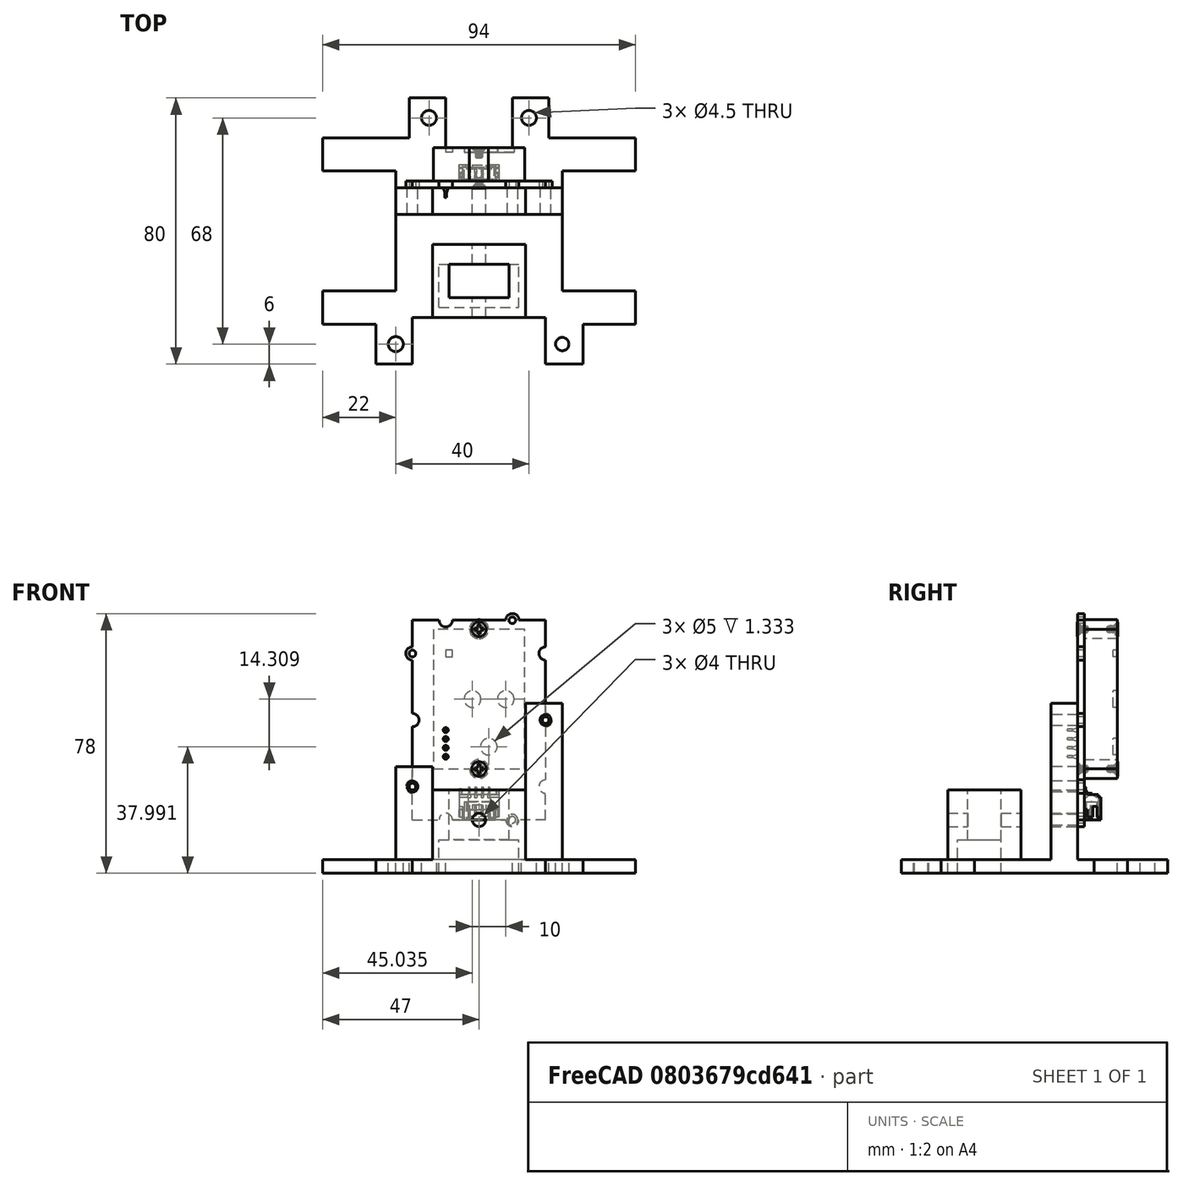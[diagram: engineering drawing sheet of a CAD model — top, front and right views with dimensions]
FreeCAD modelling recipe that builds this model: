
FCSTD DOCUMENT  (FreeCAD 0.20R29177 (Git))
Label: spin07012022
License: All rights reserved
LicenseURL: http://en.wikipedia.org/wiki/All_rights_reserved
objects: Part::Box×15, Part::Cylinder×9, Part::MultiFuse×5, Part::Cut×3, Part::Feature×1
note: 33 computed .brp shape members not serialized (recipe doc carries the construction recipe); baked Part::Feature solids carry a one-line shape summary decoded from their .brp

FEATURE [Part::Cylinder] Cylinder103  label="Cylinder107"
  Angle = 360
  AttacherType = Attacher::AttachEngine3D
  FirstAngle = 0
  Height = 10
  Placement = pos=(62,3,0) rot=(0,0,1;0rad)
  Radius = 2.25
  SecondAngle = 0
FEATURE [Part::Box] Box064  label="base005"
  AttacherType = Attacher::AttachEngine3D
  Height = 4
  Length = 26
  Placement = pos=(-10.25,68,0) rot=(0,0,1;0rad)
  Width = 12
FEATURE [Part::Box] Box060  label="base001"
  AttacherType = Attacher::AttachEngine3D
  Height = 4
  Length = 94
  Width = 80
FEATURE [Part::Box] Box061  label="base002"
  AttacherType = Attacher::AttachEngine3D
  Height = 4
  Length = 26
  Width = 12
FEATURE [Part::Box] Box062  label="base003"
  AttacherType = Attacher::AttachEngine3D
  Height = 4
  Length = 26
  Placement = pos=(68,0,0) rot=(0,0,1;0rad)
  Width = 12
FEATURE [Part::Cylinder] Cylinder104  label="Cylinder103"
  Angle = 360
  AttacherType = Attacher::AttachEngine3D
  FirstAngle = 0
  Height = 10
  Placement = pos=(72,71,0) rot=(0,0,1;0rad)
  Radius = 2.25
  SecondAngle = 0
FEATURE [Part::Cylinder] Cylinder106  label="Cylinder104"
  Angle = 360
  AttacherType = Attacher::AttachEngine3D
  FirstAngle = 0
  Height = 10
  Placement = pos=(22,71,0) rot=(0,0,1;0rad)
  Radius = 2
  SecondAngle = 0
FEATURE [Part::Cylinder] Cylinder105  label="Cylinder108"
  Angle = 360
  AttacherType = Attacher::AttachEngine3D
  FirstAngle = 0
  Height = 10
  Placement = pos=(32,3,0) rot=(0,0,1;0rad)
  Radius = 2.25
  SecondAngle = 0
FEATURE [Part::Box] Box081  label="Cube039"
  AttacherType = Attacher::AttachEngine3D
  Height = 10
  Length = 25
  Placement = pos=(85,26,140) rot=(0,0,1;0rad)
  Width = 36
FEATURE [Part::Box] Box082  label="Cube040"
  AttacherType = Attacher::AttachEngine3D
  Height = 10
  Length = 40
  Placement = pos=(40,1,140) rot=(0,0,1;0rad)
  Width = 17
FEATURE [Part::Box] Box073  label="baseSpineCut"
  AttacherType = Attacher::AttachEngine3D
  Height = 25
  Length = 18
  Placement = pos=(51,24,140) rot=(0,0,1;0rad)
  Width = 10
FEATURE [Part::Cylinder] Cylinder107  label="Cylinder109"
  Angle = 360
  AttacherType = Attacher::AttachEngine3D
  FirstAngle = 0
  Height = 10
  Radius = 1
  SecondAngle = 0
FEATURE [Part::MultiFuse] Fusion123  label="screwIns001"
  Placement = pos=(0,3,0) rot=(0,0,1;0rad)
  Shapes = -> [Cylinder105,Cylinder107,Cylinder103,Cylinder104,Cylinder106]
FEATURE [Part::Box] Box080  label="Cube038"
  AttacherType = Attacher::AttachEngine3D
  Height = 10
  Length = 22
  Placement = pos=(13,26,140) rot=(0,0,1;0rad)
  Width = 36
FEATURE [Part::Box] Box063  label="base004"
  AttacherType = Attacher::AttachEngine3D
  Height = 4
  Length = 26
  Placement = pos=(78,68,0) rot=(0,0,1;0rad)
  Width = 12
FEATURE [Part::MultiFuse] Fusion122
  Shapes = -> [Box064,Box063,Box061,Box062]
FEATURE [Part::Cut] Cut019  label="baseNew"
  Base = -> Box060
  Tool = -> Fusion122
FEATURE [Part::Cut] Cut020  label="baseNew001"
  Base = -> Cut019
  Placement = pos=(107,84,140) rot=(0,0,1;3.14159rad)
  Tool = -> Fusion123
FEATURE [Part::Box] Box083  label="Cube041"
  AttacherType = Attacher::AttachEngine3D
  Height = 10
  Length = 24
  Placement = pos=(48,21,140) rot=(0,0,1;0rad)
  Width = 13
FEATURE [Part::Box] Box084  label="Cube042"
  AttacherType = Attacher::AttachEngine3D
  Height = 51
  Length = 50
  Placement = pos=(35,49,140) rot=(0,0,1;0rad)
  Width = 8
FEATURE [Part::Box] Box085  label="Cube043"
  AttacherType = Attacher::AttachEngine3D
  Height = 10
  Length = 15
  Placement = pos=(70,69,140) rot=(0,0,1;1.5708rad)
  Width = 20
FEATURE [Part::Box] Box086  label="baseSpineIn"
  AttacherType = Attacher::AttachEngine3D
  Height = 25
  Length = 28
  Placement = pos=(46,18,140) rot=(0,0,1;0rad)
  Width = 22
FEATURE [Part::Cylinder] Cylinder
  Angle = 360
  AttacherType = Attacher::AttachEngine3D
  FirstAngle = 0
  Height = 50
  Placement = pos=(60,17,156) rot=(-1,0,0;1.5708rad)
  Radius = 2
  SecondAngle = 0
FEATURE [Part::Feature] Feature  label="Seed Grove SCD30"
  Placement = pos=(40,59,156) rot=(0.707107,0,0.707107;3.14159rad)
  shape: bbox 44 x 15.1 x 64 mm, 422 faces, 13 solids (baked)
FEATURE [Part::Cylinder] Cylinder108  label="Cylinder110"
  Angle = 360
  AttacherType = Attacher::AttachEngine3D
  FirstAngle = 0
  Height = 50
  Placement = pos=(80,17,186) rot=(-1,0,0;1.5708rad)
  Radius = 1.65
  SecondAngle = 0
FEATURE [Part::Cylinder] Cylinder109  label="Cylinder111"
  Angle = 360
  AttacherType = Attacher::AttachEngine3D
  FirstAngle = 0
  Height = 50
  Placement = pos=(40,17,166) rot=(-1,0,0;1.5708rad)
  Radius = 1.65
  SecondAngle = 0
FEATURE [Part::Cylinder] Cylinder110  label="Cylinder112"
  Angle = 360
  AttacherType = Attacher::AttachEngine3D
  FirstAngle = 0
  Height = 50
  Placement = pos=(70,17,156) rot=(-1,0,0;1.5708rad)
  Radius = 1.65
  SecondAngle = 0
FEATURE [Part::MultiFuse] Fusion  label="m2Cuts"
  Placement = pos=(0,30,0) rot=(0,0,1;0rad)
  Shapes = -> [Cylinder108,Cylinder109,Cylinder110]
FEATURE [Part::Box] Box087  label="Cube044"
  AttacherType = Attacher::AttachEngine3D
  Height = 51
  Length = 50
  Placement = pos=(21,49,172) rot=(0,0,1;0rad)
  Width = 8
FEATURE [Part::Box] Box088  label="Cube045"
  AttacherType = Attacher::AttachEngine3D
  Height = 51
  Length = 28
  Placement = pos=(46,49,165) rot=(0,0,1;0rad)
  Width = 8
FEATURE [Part::MultiFuse] Fusion124
  Shapes = -> [Cut020,Box084,Box086]
FEATURE [Part::MultiFuse] Fusion125
  Shapes = -> [Box087,Box088,Fusion,Box085,Box080,Box083,Box082,Box081,Box073,Cylinder]
FEATURE [Part::Cut] Cut  label="allIn"
  Base = -> Fusion124
  Tool = -> Fusion125
